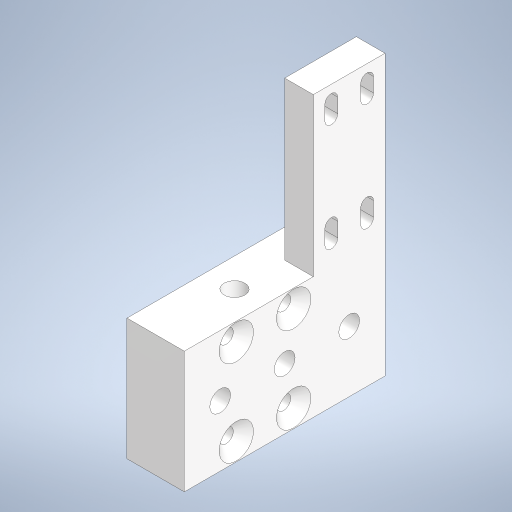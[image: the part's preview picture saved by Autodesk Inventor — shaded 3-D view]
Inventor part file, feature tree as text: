
AUTODESK INVENTOR PART (.ipt)
format: ipt  version: 2024.1 (Build 281209000, 209)  size: 366,592 bytes
history: native  units: in
note: dims shown in document units (in); Inventor stores cm internally (conversion verified against a paired STEP export)
features: extrude x7, sketch x7, chamfer x2
ambient origin geometry x8: Origin, YZ Plane, XZ Plane, XY Plane, X Axis, Y Axis, Z Axis, Center Point
bodies: Solid1 (feature_tree)
feature tree (16):
  extrude  "Extrusion1"  Depth=1.1024in
  extrude  "Extrusion2"  Depth=0.3937in
  extrude  "Extrusion3"  Depth=0.315in TaperAngle=0.0deg
  extrude  "Extrusion4"  TaperAngle=0.0deg  [1 undecoded]
  extrude  "Extrusion5"  Depth=0.0787in
  chamfer  "Chamfer1"  Distance=0.0984in
  extrude  "Extrusion7"  Depth=0.0354in
  chamfer  "Chamfer3"  Distance=0.0984in
  extrude  "Extrusion8"  Depth=0.0354in
  sketch  "Sketch1"  dims[d0=0.6693in d1=1.1024in]
  sketch  "Sketch2"  dims[d2=0.315in d3=0.0in d4=0.3937in]
  sketch  "Sketch3"  dims[d5=0.8661in d6=0.315in d7=0.0in]
  sketch  "Sketch4"  dims[d8=0.1575in d9=0.0in d10=0.0in]
  sketch  "Sketch5"  dims[d11=0.0787in d13=0.0787in]
  sketch  "Sketch8"  dims[d14=0.0787in]
  sketch  "Sketch9"  dims[d15=0.0787in d16=0.0984in d17=0.0984in d18=0.0984in d19=0.0984in d20=0.2854in d21=0.2854in d22=0.315in d23=0.315in d24=0.0in d25=0.0in d26=0.1142in d27=0.1142in d28=0.1575in d29=0.1575in d30=0.6693in d31=0.0in d32=0.0in d33=0.0079in d34=0.0787in d35=45.0deg d53=0.3346in d54=0.3346in d55=0.3346in d56=0.1142in d57=0.1142in d58=0.1142in d59=0.1969in d60=0.5512in d61=0.1969in d62=0.0in d63=0.0in d64=0.0551in d65=0.0787in d66=45.0deg d70=0.0709in d71=0.0709in d72=0.0709in d73=0.0709in d74=0.0984in d75=0.0787in d76=0.0787in d77=0.0984in d78=0.0984in d79=0.0984in d80=0.5906in d81=0.5906in d82=0.0709in d83=0.0709in d84=0.0709in d85=0.0787in d86=0.0787in d87=0.0787in d88=0.0354in d89=0.0354in d90=0.0in d91=0.0in]
note: 1 required parameter value undecoded (feature->parameter linkage not recoverable at this tier; creation-order binding heuristic only, values carry confidence <= 0.55)
